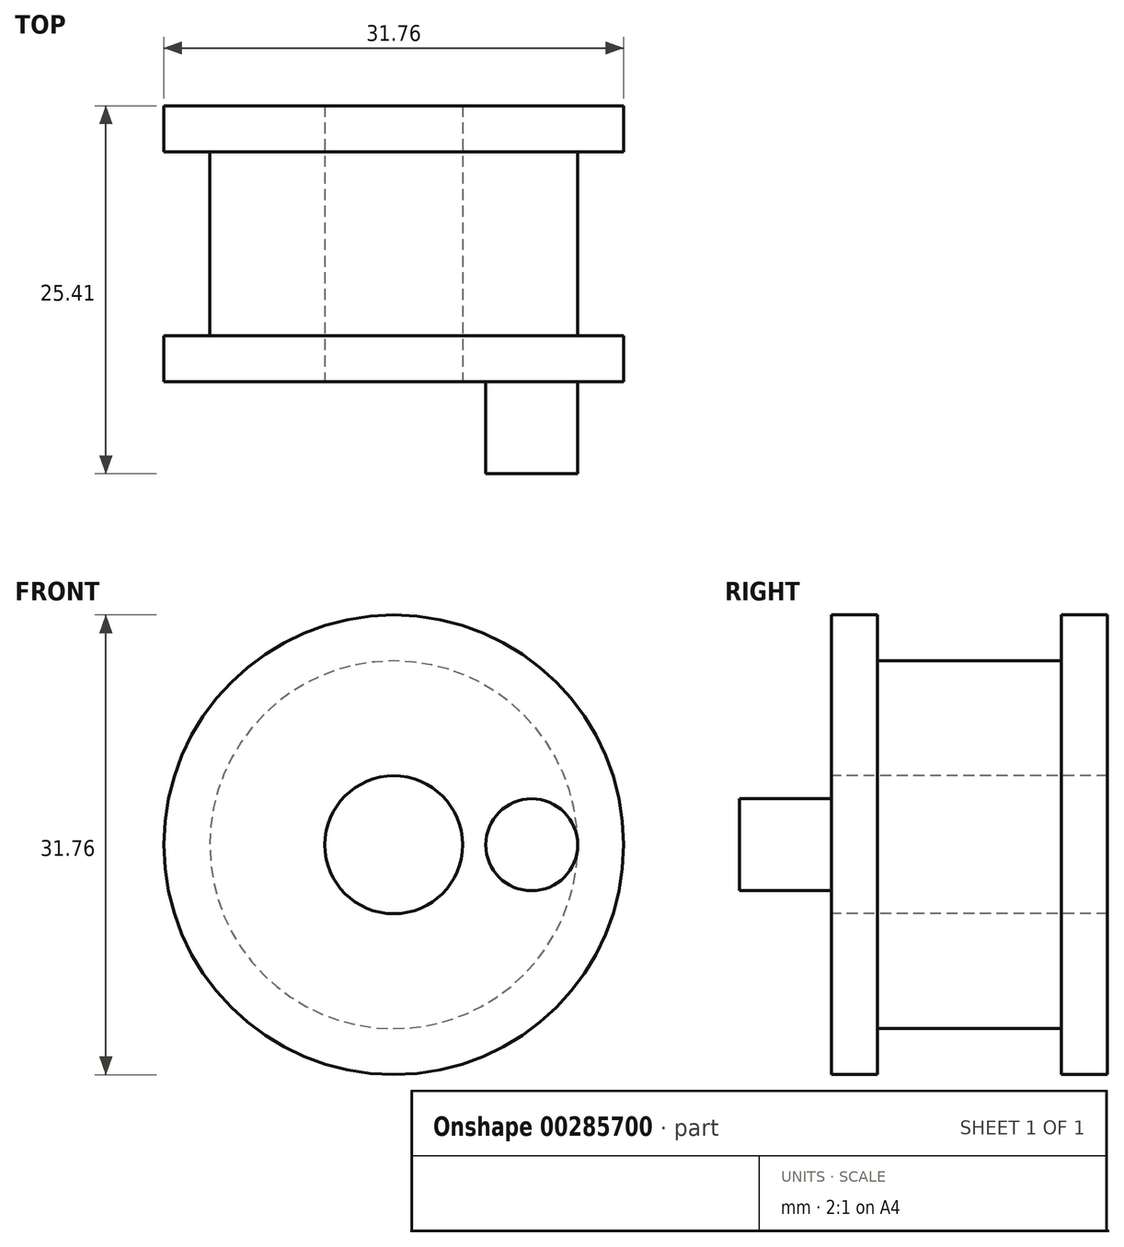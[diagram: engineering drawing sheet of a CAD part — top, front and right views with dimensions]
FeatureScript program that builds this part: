
annotation { "Feature Type Name" : "Feature", "Feature Type Description" : "" }
export const myFeature = defineFeature(function(context is Context, id is Id, definition is map)
    precondition{}
    {
        {
            var Q0;
            Q0=qCreatedBy(makeId("Top.planeOp"),FACE);
            var sketch = newSketch(context, id + "F0", { "sketchPlane" : qUnion([Q0])});
            skLineSegment(sketch, "E0", {"start": v(0, 0) * mm, "end": v(4.76, 0) * mm});
            skLineSegment(sketch, "E1.bottom", {"start": v(4.76, 0) * mm, "end": v(12.7, 0) * mm});
            skLineSegment(sketch, "E1.top", {"start": v(4.76, 12.7) * mm, "end": v(12.7, 12.7) * mm});
            skLineSegment(sketch, "E1.left", {"start": v(4.76, 0) * mm, "end": v(4.76, 12.7) * mm});
            skLineSegment(sketch, "E1.right", {"start": v(12.7, 0) * mm, "end": v(12.7, 12.7) * mm});
            skLineSegment(sketch, "E2.bottom", {"start": v(4.76, 12.7) * mm, "end": v(15.88, 12.7) * mm});
            skLineSegment(sketch, "E2.top", {"start": v(4.76, 15.88) * mm, "end": v(15.88, 15.88) * mm});
            skLineSegment(sketch, "E2.left", {"start": v(4.76, 12.7) * mm, "end": v(4.76, 15.88) * mm});
            skLineSegment(sketch, "E2.right", {"start": v(15.88, 12.7) * mm, "end": v(15.88, 15.88) * mm});
            skLineSegment(sketch, "E3.bottom", {"start": v(4.76, 0) * mm, "end": v(15.88, 0) * mm});
            skLineSegment(sketch, "E3.top", {"start": v(4.76, -3.18) * mm, "end": v(15.88, -3.18) * mm});
            skLineSegment(sketch, "E3.left", {"start": v(4.76, 0) * mm, "end": v(4.76, -3.18) * mm});
            skLineSegment(sketch, "E3.right", {"start": v(15.88, 0) * mm, "end": v(15.88, -3.18) * mm});
            skLineSegment(sketch, "E4", {"start": v(0, 0) * mm, "end": v(0, 34.83) * mm});
            skSolve(sketch);
        }
        {
            var Q0;
            Q0=makeQuery(id+"F0.imprint","IMPRINT",FACE,{"disambiguationData":[TD([[makeQuery(id+"F0.imprint","IMPRINT",EDGE,{"derivedFrom":sQuery(id+"F0.wireOp",EDGE,"E3.top")}),1.0]])]});
            var Q1;
            {var subQ0=sQuery(id+"F0.wireOp",EDGE,"E1.left");Q1=makeQuery(id+"F0.imprint","IMPRINT",FACE,{"disambiguationData":[TD([[makeQuery(id+"F0.imprint","IMPRINT",EDGE,{"derivedFrom":subQ0}),-1.0]])]});}
            var Q2;
            Q2=makeQuery(id+"F0.imprint","IMPRINT",FACE,{"disambiguationData":[TD([[makeQuery(id+"F0.imprint","IMPRINT",EDGE,{"derivedFrom":sQuery(id+"F0.wireOp",EDGE,"E2.top")}),-1.0]])]});
            var Q3;
            Q3=sQuery(id+"F0.wireOp",EDGE,"E4");
            revolve(context, id + "F1", {"entities" : qUnion([Q0, Q1, Q2]), "axis" : qUnion([Q3]), "revolveType" : RevolveType.FULL});
        }
        {
            var Q0;
            Q0=makeQuery(id+"F1.opRevolve","SWEPT_FACE",FACE,{"disambiguationData":[OSD([sQuery(id+"F0.wireOp",EDGE,"E3.top")])]});
            var sketch = newSketch(context, id + "F2", { "sketchPlane" : qUnion([Q0])});
            skCircle(sketch, "E5", {"center": v(9.53, 0) * mm, "radius": 3.18 * mm});
            skSolve(sketch);
        }
        {
            var Q0;
            Q0=makeQuery(id+"F2.imprint","IMPRINT",FACE,{"disambiguationData":[TD([[makeQuery(id+"F2.imprint","IMPRINT",EDGE,{"derivedFrom":sQuery(id+"F2.wireOp",EDGE,"E5")}),1.0]])]});
            extrude(context, id + "F3", {"entities" : qUnion([Q0]), "operationType" : NewBodyOperationType.ADD, "depth" : 6.35 * mm});
        }
    });
